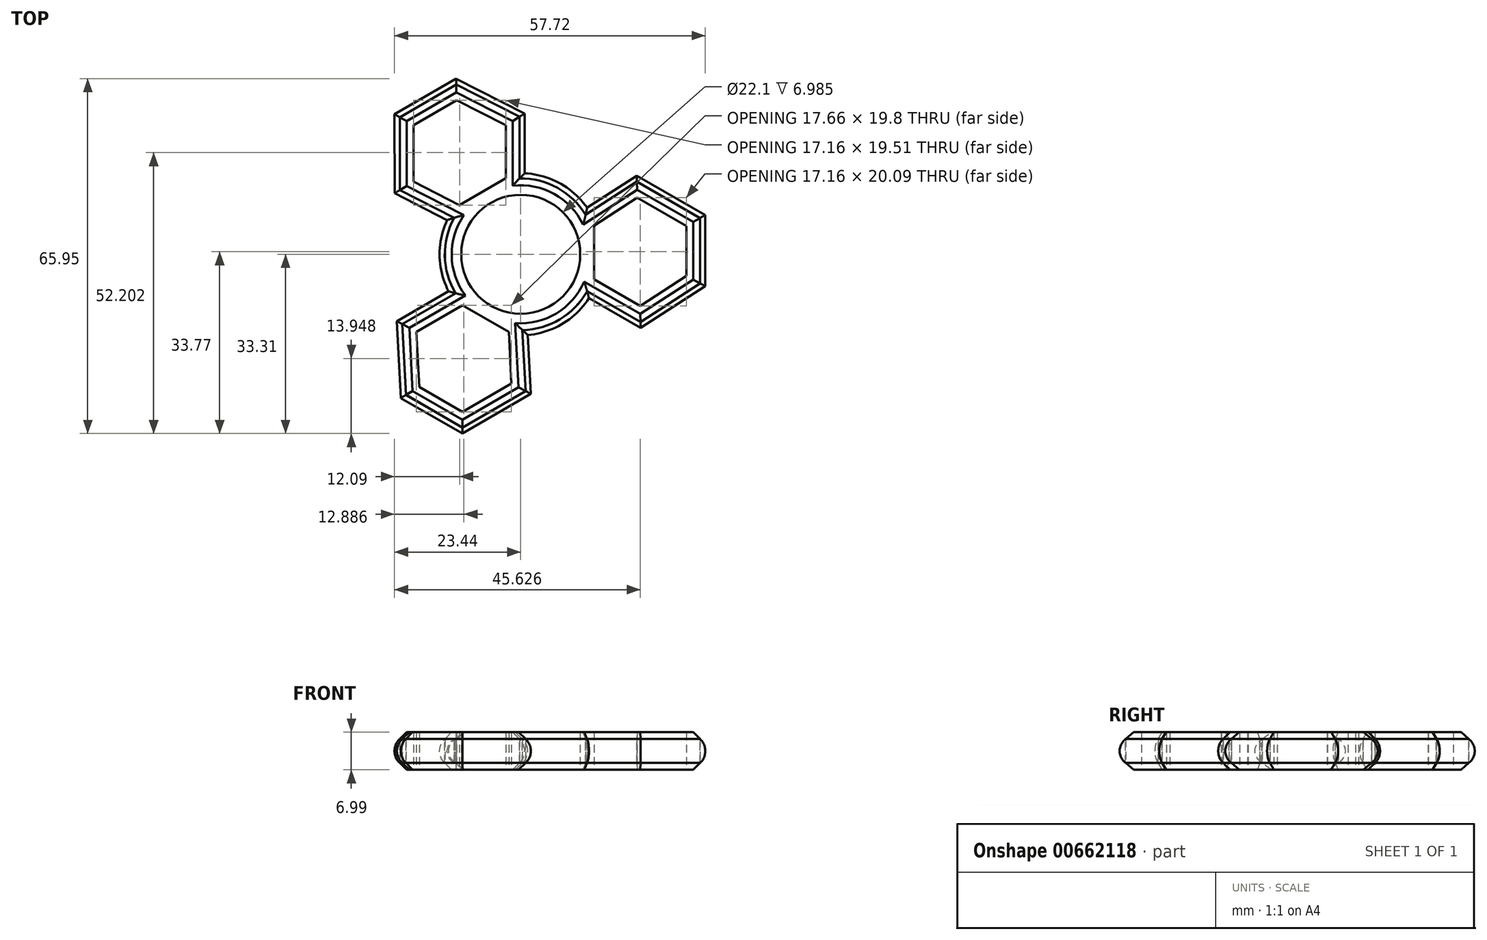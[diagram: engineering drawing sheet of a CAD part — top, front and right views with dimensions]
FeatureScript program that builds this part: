
annotation { "Feature Type Name" : "Feature", "Feature Type Description" : "" }
export const myFeature = defineFeature(function(context is Context, id is Id, definition is map)
    precondition{}
    {
        {
            var Q0;
            Q0=qCreatedBy(makeId("Top.planeOp"),FACE);
            var sketch = newSketch(context, id + "F0", { "sketchPlane" : qUnion([Q0])});
            skCircle(sketch, "E0", {"center": v(0, 0) * mm, "radius": 11.05 * mm});
            skLineSegment(sketch, "E1.0", {"start": v(21.64, 10.5) * mm, "end": v(30.75, 5.26) * mm});
            skLineSegment(sketch, "E1.1", {"start": v(30.75, 5.26) * mm, "end": v(30.76, -4.01) * mm});
            skLineSegment(sketch, "E1.2", {"start": v(30.76, -4.01) * mm, "end": v(22.17, -9.58) * mm});
            skLineSegment(sketch, "E1.3", {"start": v(22.17, -9.58) * mm, "end": v(13.62, -4.66) * mm});
            skLineSegment(sketch, "E1.4", {"start": v(13.62, -4.66) * mm, "end": v(13.6, 5.3) * mm});
            skLineSegment(sketch, "E1.5", {"start": v(13.6, 5.3) * mm, "end": v(21.64, 10.5) * mm});
            skLineSegment(sketch, "E2.1.0", {"start": v(-11.4, 9.14) * mm, "end": v(-19.92, 13.49) * mm});
            skLineSegment(sketch, "E2.1.1", {"start": v(-2.77, 14.13) * mm, "end": v(-11.4, 9.14) * mm});
            skLineSegment(sketch, "E2.1.2", {"start": v(-2.78, 24) * mm, "end": v(-2.77, 14.13) * mm});
            skLineSegment(sketch, "E2.1.3", {"start": v(-11.9, 28.65) * mm, "end": v(-2.78, 24) * mm});
            skLineSegment(sketch, "E2.1.4", {"start": v(-19.93, 24) * mm, "end": v(-11.9, 28.65) * mm});
            skLineSegment(sketch, "E2.1.5", {"start": v(-19.92, 13.49) * mm, "end": v(-19.93, 24) * mm});
            skLineSegment(sketch, "E2.2.0", {"start": v(-2.22, -14.43) * mm, "end": v(-1.72, -24) * mm});
            skLineSegment(sketch, "E2.2.1", {"start": v(-10.85, -9.46) * mm, "end": v(-2.22, -14.43) * mm});
            skLineSegment(sketch, "E2.2.2", {"start": v(-19.38, -14.4) * mm, "end": v(-10.85, -9.46) * mm});
            skLineSegment(sketch, "E2.2.3", {"start": v(-18.86, -24.64) * mm, "end": v(-19.38, -14.4) * mm});
            skLineSegment(sketch, "E2.2.4", {"start": v(-10.82, -29.26) * mm, "end": v(-18.86, -24.64) * mm});
            skLineSegment(sketch, "E2.2.5", {"start": v(-1.72, -24) * mm, "end": v(-10.82, -29.26) * mm});
            skLineSegment(sketch, "E3.0", {"start": v(21.56, 13.48) * mm, "end": v(33.3, 6.73) * mm});
            skLineSegment(sketch, "E3.1", {"start": v(33.3, -5.4) * mm, "end": v(22.25, -12.56) * mm});
            skLineSegment(sketch, "E3.2", {"start": v(22.25, -12.56) * mm, "end": v(12.32, -6.85) * mm});
            skLineSegment(sketch, "E3.3", {"start": v(33.3, 6.73) * mm, "end": v(33.3, -5.4) * mm});
            skLineSegment(sketch, "E3.5", {"start": v(12.05, 7.32) * mm, "end": v(21.56, 13.48) * mm});
            skLineSegment(sketch, "E4.0", {"start": v(-21.32, -26.15) * mm, "end": v(-22, -12.99) * mm});
            skLineSegment(sketch, "E4.2", {"start": v(0.31, -14.1) * mm, "end": v(0.9, -25.41) * mm});
            skLineSegment(sketch, "E4.3", {"start": v(-22, -12.99) * mm, "end": v(-12.1, -7.25) * mm});
            skLineSegment(sketch, "E4.4", {"start": v(0.9, -25.41) * mm, "end": v(-10.82, -32.2) * mm});
            skLineSegment(sketch, "E4.5", {"start": v(-10.82, -32.2) * mm, "end": v(-21.32, -26.15) * mm});
            skLineSegment(sketch, "E5.0", {"start": v(-11.98, 31.54) * mm, "end": v(-0.25, 25.55) * mm});
            skLineSegment(sketch, "E5.2", {"start": v(-12.36, 6.78) * mm, "end": v(-22.45, 11.93) * mm});
            skLineSegment(sketch, "E5.3", {"start": v(-0.25, 25.55) * mm, "end": v(-0.23, 14.1) * mm});
            skLineSegment(sketch, "E5.4", {"start": v(-22.45, 11.93) * mm, "end": v(-22.47, 25.47) * mm});
            skLineSegment(sketch, "E5.5", {"start": v(-22.47, 25.47) * mm, "end": v(-11.98, 31.54) * mm});
            skArc(sketch, "E6.0", {"start": v(12.05, 7.32) * mm, "mid": v(6.81, 12.34) * mm, "end": v(-0.23, 14.1) * mm});
            skArc(sketch, "E7.trimOffspring", {"start": v(0.31, -14.1) * mm, "mid": v(7.28, -12.07) * mm, "end": v(12.32, -6.85) * mm});
            skArc(sketch, "E8.trimOffspring", {"start": v(-12.36, 6.78) * mm, "mid": v(-14.1, -0.27) * mm, "end": v(-12.1, -7.25) * mm});
            skSolve(sketch);
        }
        {
            var Q0;
            Q0=makeQuery(id+"F0.imprint","IMPRINT",FACE,{"disambiguationData":[TD([[makeQuery(id+"F0.imprint","IMPRINT",EDGE,{"derivedFrom":sQuery(id+"F0.wireOp",EDGE,"E0")}),-1.0]])]});
            extrude(context, id + "F1", {"entities" : qUnion([Q0]), "depth" : 7 * mm, "offsetDistance" : 25.4 * mm});
        }
        {
            var Q0;
            Q0=makeQuery(id+"F1.opExtrude","CAP_EDGE",EDGE,{"disambiguationData":[OSD([sQuery(id+"F0.wireOp",EDGE,"E4.5")])],"isStart":false});
            var Q1;
            Q1=makeQuery(id+"F1.opExtrude","CAP_EDGE",EDGE,{"disambiguationData":[OSD([sQuery(id+"F0.wireOp",EDGE,"E4.4")])],"isStart":false});
            var Q2;
            Q2=makeQuery(id+"F1.opExtrude","CAP_EDGE",EDGE,{"disambiguationData":[OSD([sQuery(id+"F0.wireOp",EDGE,"E4.2")])],"isStart":false});
            var Q3;
            Q3=makeQuery(id+"F1.opExtrude","CAP_EDGE",EDGE,{"disambiguationData":[OSD([sQuery(id+"F0.wireOp",EDGE,"E7.trimOffspring")])],"isStart":false});
            var Q4;
            Q4=makeQuery(id+"F1.opExtrude","CAP_EDGE",EDGE,{"disambiguationData":[OSD([sQuery(id+"F0.wireOp",EDGE,"E3.2")])],"isStart":false});
            var Q5;
            Q5=makeQuery(id+"F1.opExtrude","CAP_EDGE",EDGE,{"disambiguationData":[OSD([sQuery(id+"F0.wireOp",EDGE,"E3.1")])],"isStart":false});
            var Q6;
            Q6=makeQuery(id+"F1.opExtrude","CAP_EDGE",EDGE,{"disambiguationData":[OSD([sQuery(id+"F0.wireOp",EDGE,"E3.3")])],"isStart":false});
            var Q7;
            Q7=makeQuery(id+"F1.opExtrude","CAP_EDGE",EDGE,{"disambiguationData":[OSD([sQuery(id+"F0.wireOp",EDGE,"E3.0")])],"isStart":false});
            var Q8;
            Q8=makeQuery(id+"F1.opExtrude","CAP_EDGE",EDGE,{"disambiguationData":[OSD([sQuery(id+"F0.wireOp",EDGE,"E3.5")])],"isStart":false});
            var Q9;
            Q9=makeQuery(id+"F1.opExtrude","CAP_EDGE",EDGE,{"disambiguationData":[OSD([sQuery(id+"F0.wireOp",EDGE,"E6.0")])],"isStart":false});
            var Q10;
            Q10=makeQuery(id+"F1.opExtrude","CAP_EDGE",EDGE,{"disambiguationData":[OSD([sQuery(id+"F0.wireOp",EDGE,"E5.3")])],"isStart":false});
            var Q11;
            Q11=makeQuery(id+"F1.opExtrude","CAP_EDGE",EDGE,{"disambiguationData":[OSD([sQuery(id+"F0.wireOp",EDGE,"E5.0")])],"isStart":false});
            var Q12;
            Q12=makeQuery(id+"F1.opExtrude","CAP_EDGE",EDGE,{"disambiguationData":[OSD([sQuery(id+"F0.wireOp",EDGE,"E5.5")])],"isStart":false});
            var Q13;
            Q13=makeQuery(id+"F1.opExtrude","CAP_EDGE",EDGE,{"disambiguationData":[OSD([sQuery(id+"F0.wireOp",EDGE,"E5.4")])],"isStart":false});
            var Q14;
            Q14=makeQuery(id+"F1.opExtrude","CAP_EDGE",EDGE,{"disambiguationData":[OSD([sQuery(id+"F0.wireOp",EDGE,"E5.2")])],"isStart":false});
            var Q15;
            Q15=makeQuery(id+"F1.opExtrude","CAP_EDGE",EDGE,{"disambiguationData":[OSD([sQuery(id+"F0.wireOp",EDGE,"E8.trimOffspring")])],"isStart":false});
            var Q16;
            Q16=makeQuery(id+"F1.opExtrude","CAP_EDGE",EDGE,{"disambiguationData":[OSD([sQuery(id+"F0.wireOp",EDGE,"E4.3")])],"isStart":false});
            var Q17;
            Q17=makeQuery(id+"F1.opExtrude","CAP_EDGE",EDGE,{"disambiguationData":[OSD([sQuery(id+"F0.wireOp",EDGE,"E4.0")])],"isStart":false});
            chamfer(context, id + "F2", {"entities" : qUnion([Q0, Q1, Q2, Q3, Q4, Q5, Q6, Q7, Q8, Q9, Q10, Q11, Q12, Q13, Q14, Q15, Q16, Q17]), "width" : 1.27 * mm, "tangentPropagation" : true});
        }
        {
            var Q0;
            Q0=makeQuery(id+"F1.opExtrude","CAP_EDGE",EDGE,{"disambiguationData":[OSD([sQuery(id+"F0.wireOp",EDGE,"E5.4")])],"isStart":true});
            var Q1;
            Q1=makeQuery(id+"F1.opExtrude","CAP_EDGE",EDGE,{"disambiguationData":[OSD([sQuery(id+"F0.wireOp",EDGE,"E5.5")])],"isStart":true});
            var Q2;
            Q2=makeQuery(id+"F1.opExtrude","CAP_EDGE",EDGE,{"disambiguationData":[OSD([sQuery(id+"F0.wireOp",EDGE,"E5.2")])],"isStart":true});
            var Q3;
            Q3=makeQuery(id+"F1.opExtrude","CAP_EDGE",EDGE,{"disambiguationData":[OSD([sQuery(id+"F0.wireOp",EDGE,"E8.trimOffspring")])],"isStart":true});
            var Q4;
            Q4=makeQuery(id+"F1.opExtrude","CAP_EDGE",EDGE,{"disambiguationData":[OSD([sQuery(id+"F0.wireOp",EDGE,"E4.3")])],"isStart":true});
            var Q5;
            Q5=makeQuery(id+"F1.opExtrude","CAP_EDGE",EDGE,{"disambiguationData":[OSD([sQuery(id+"F0.wireOp",EDGE,"E4.0")])],"isStart":true});
            var Q6;
            Q6=makeQuery(id+"F1.opExtrude","CAP_EDGE",EDGE,{"disambiguationData":[OSD([sQuery(id+"F0.wireOp",EDGE,"E5.0")])],"isStart":true});
            var Q7;
            Q7=makeQuery(id+"F1.opExtrude","CAP_EDGE",EDGE,{"disambiguationData":[OSD([sQuery(id+"F0.wireOp",EDGE,"E5.3")])],"isStart":true});
            var Q8;
            Q8=makeQuery(id+"F1.opExtrude","CAP_EDGE",EDGE,{"disambiguationData":[OSD([sQuery(id+"F0.wireOp",EDGE,"E6.0")])],"isStart":true});
            var Q9;
            Q9=makeQuery(id+"F1.opExtrude","CAP_EDGE",EDGE,{"disambiguationData":[OSD([sQuery(id+"F0.wireOp",EDGE,"E3.5")])],"isStart":true});
            var Q10;
            Q10=makeQuery(id+"F1.opExtrude","CAP_EDGE",EDGE,{"disambiguationData":[OSD([sQuery(id+"F0.wireOp",EDGE,"E3.0")])],"isStart":true});
            var Q11;
            Q11=makeQuery(id+"F1.opExtrude","CAP_EDGE",EDGE,{"disambiguationData":[OSD([sQuery(id+"F0.wireOp",EDGE,"E3.3")])],"isStart":true});
            var Q12;
            Q12=makeQuery(id+"F1.opExtrude","CAP_EDGE",EDGE,{"disambiguationData":[OSD([sQuery(id+"F0.wireOp",EDGE,"E3.1")])],"isStart":true});
            var Q13;
            Q13=makeQuery(id+"F1.opExtrude","CAP_EDGE",EDGE,{"disambiguationData":[OSD([sQuery(id+"F0.wireOp",EDGE,"E3.2")])],"isStart":true});
            var Q14;
            Q14=makeQuery(id+"F1.opExtrude","CAP_EDGE",EDGE,{"disambiguationData":[OSD([sQuery(id+"F0.wireOp",EDGE,"E7.trimOffspring")])],"isStart":true});
            var Q15;
            Q15=makeQuery(id+"F1.opExtrude","CAP_EDGE",EDGE,{"disambiguationData":[OSD([sQuery(id+"F0.wireOp",EDGE,"E4.2")])],"isStart":true});
            var Q16;
            Q16=makeQuery(id+"F1.opExtrude","CAP_EDGE",EDGE,{"disambiguationData":[OSD([sQuery(id+"F0.wireOp",EDGE,"E4.4")])],"isStart":true});
            var Q17;
            Q17=makeQuery(id+"F1.opExtrude","CAP_EDGE",EDGE,{"disambiguationData":[OSD([sQuery(id+"F0.wireOp",EDGE,"E4.5")])],"isStart":true});
            chamfer(context, id + "F3", {"entities" : qUnion([Q0, Q1, Q2, Q3, Q4, Q5, Q6, Q7, Q8, Q9, Q10, Q11, Q12, Q13, Q14, Q15, Q16, Q17]), "width" : 1.27 * mm, "tangentPropagation" : true});
        }
        {
            var Q0;
            Q0=qCreatedBy(makeId("Front.planeOp"),FACE);
            var sketch = newSketch(context, id + "F4", { "sketchPlane" : qUnion([Q0])});
            skArc(sketch, "E9", {"start": v(33.3, 1.27) * mm, "mid": v(34.27, 3.5) * mm, "end": v(33.3, 5.71) * mm});
            skLineSegment(sketch, "E10", {"start": v(33.3, 5.71) * mm, "end": v(33.3, 1.27) * mm});
            skSolve(sketch);
        }
        {
            var Q0;
            Q0=makeQuery(id+"F4.imprint","IMPRINT",FACE,{"disambiguationData":[TD([[makeQuery(id+"F4.imprint","IMPRINT",EDGE,{"derivedFrom":sQuery(id+"F4.wireOp",EDGE,"E9")}),1.0]])]});
            var Q1;
            {var subQ0=sQuery(id+"F0.wireOp",EDGE,"E3.3");Q1=makeQuery(id+"F2.opChamfer","BLEND_EDGE",EDGE,{"blendedFrom":[makeQuery(id+"F1.opExtrude","CAP_EDGE",EDGE,{"disambiguationData":[OSD([subQ0])],"isStart":false}),makeQuery(id+"F1.opExtrude","SWEPT_FACE",FACE,{"disambiguationData":[OSD([subQ0])]})],"blendedInto":[makeQuery(id+"F1.opExtrude","SWEPT_FACE",FACE,{"disambiguationData":[OSD([subQ0])]})]});}
            var Q2;
            {var subQ0=sQuery(id+"F0.wireOp",EDGE,"E3.1");Q2=makeQuery(id+"F2.opChamfer","BLEND_EDGE",EDGE,{"blendedFrom":[makeQuery(id+"F1.opExtrude","CAP_EDGE",EDGE,{"disambiguationData":[OSD([subQ0])],"isStart":false}),makeQuery(id+"F1.opExtrude","SWEPT_FACE",FACE,{"disambiguationData":[OSD([subQ0])]})],"blendedInto":[makeQuery(id+"F1.opExtrude","SWEPT_FACE",FACE,{"disambiguationData":[OSD([subQ0])]})]});}
            var Q3;
            {var subQ0=sQuery(id+"F0.wireOp",EDGE,"E3.2");Q3=makeQuery(id+"F2.opChamfer","BLEND_EDGE",EDGE,{"blendedFrom":[makeQuery(id+"F1.opExtrude","CAP_EDGE",EDGE,{"disambiguationData":[OSD([subQ0])],"isStart":false}),makeQuery(id+"F1.opExtrude","SWEPT_FACE",FACE,{"disambiguationData":[OSD([subQ0])]})],"blendedInto":[makeQuery(id+"F1.opExtrude","SWEPT_FACE",FACE,{"disambiguationData":[OSD([subQ0])]})]});}
            var Q4;
            {var subQ0=sQuery(id+"F0.wireOp",EDGE,"E7.trimOffspring");Q4=makeQuery(id+"F2.opChamfer","BLEND_EDGE",EDGE,{"blendedFrom":[makeQuery(id+"F1.opExtrude","CAP_EDGE",EDGE,{"disambiguationData":[OSD([subQ0])],"isStart":false}),makeQuery(id+"F1.opExtrude","SWEPT_FACE",FACE,{"disambiguationData":[OSD([subQ0])]})],"blendedInto":[makeQuery(id+"F1.opExtrude","SWEPT_FACE",FACE,{"disambiguationData":[OSD([subQ0])]})]});}
            var Q5;
            {var subQ0=sQuery(id+"F0.wireOp",EDGE,"E4.2");Q5=makeQuery(id+"F2.opChamfer","BLEND_EDGE",EDGE,{"blendedFrom":[makeQuery(id+"F1.opExtrude","CAP_EDGE",EDGE,{"disambiguationData":[OSD([subQ0])],"isStart":false}),makeQuery(id+"F1.opExtrude","SWEPT_FACE",FACE,{"disambiguationData":[OSD([subQ0])]})],"blendedInto":[makeQuery(id+"F1.opExtrude","SWEPT_FACE",FACE,{"disambiguationData":[OSD([subQ0])]})]});}
            var Q6;
            {var subQ0=sQuery(id+"F0.wireOp",EDGE,"E4.4");Q6=makeQuery(id+"F2.opChamfer","BLEND_EDGE",EDGE,{"blendedFrom":[makeQuery(id+"F1.opExtrude","CAP_EDGE",EDGE,{"disambiguationData":[OSD([subQ0])],"isStart":false}),makeQuery(id+"F1.opExtrude","SWEPT_FACE",FACE,{"disambiguationData":[OSD([subQ0])]})],"blendedInto":[makeQuery(id+"F1.opExtrude","SWEPT_FACE",FACE,{"disambiguationData":[OSD([subQ0])]})]});}
            var Q7;
            {var subQ0=sQuery(id+"F0.wireOp",EDGE,"E4.5");Q7=makeQuery(id+"F2.opChamfer","BLEND_EDGE",EDGE,{"blendedFrom":[makeQuery(id+"F1.opExtrude","CAP_EDGE",EDGE,{"disambiguationData":[OSD([subQ0])],"isStart":false}),makeQuery(id+"F1.opExtrude","SWEPT_FACE",FACE,{"disambiguationData":[OSD([subQ0])]})],"blendedInto":[makeQuery(id+"F1.opExtrude","SWEPT_FACE",FACE,{"disambiguationData":[OSD([subQ0])]})]});}
            var Q8;
            {var subQ0=sQuery(id+"F0.wireOp",EDGE,"E8.trimOffspring");Q8=makeQuery(id+"F2.opChamfer","BLEND_EDGE",EDGE,{"blendedFrom":[makeQuery(id+"F1.opExtrude","CAP_EDGE",EDGE,{"disambiguationData":[OSD([subQ0])],"isStart":false}),makeQuery(id+"F1.opExtrude","SWEPT_FACE",FACE,{"disambiguationData":[OSD([subQ0])]})],"blendedInto":[makeQuery(id+"F1.opExtrude","SWEPT_FACE",FACE,{"disambiguationData":[OSD([subQ0])]})]});}
            var Q9;
            {var subQ0=sQuery(id+"F0.wireOp",EDGE,"E4.3");Q9=makeQuery(id+"F2.opChamfer","BLEND_EDGE",EDGE,{"blendedFrom":[makeQuery(id+"F1.opExtrude","CAP_EDGE",EDGE,{"disambiguationData":[OSD([subQ0])],"isStart":false}),makeQuery(id+"F1.opExtrude","SWEPT_FACE",FACE,{"disambiguationData":[OSD([subQ0])]})],"blendedInto":[makeQuery(id+"F1.opExtrude","SWEPT_FACE",FACE,{"disambiguationData":[OSD([subQ0])]})]});}
            var Q10;
            {var subQ0=sQuery(id+"F0.wireOp",EDGE,"E4.0");Q10=makeQuery(id+"F2.opChamfer","BLEND_EDGE",EDGE,{"blendedFrom":[makeQuery(id+"F1.opExtrude","CAP_EDGE",EDGE,{"disambiguationData":[OSD([subQ0])],"isStart":false}),makeQuery(id+"F1.opExtrude","SWEPT_FACE",FACE,{"disambiguationData":[OSD([subQ0])]})],"blendedInto":[makeQuery(id+"F1.opExtrude","SWEPT_FACE",FACE,{"disambiguationData":[OSD([subQ0])]})]});}
            var Q11;
            {var subQ0=sQuery(id+"F0.wireOp",EDGE,"E5.2");Q11=makeQuery(id+"F2.opChamfer","BLEND_EDGE",EDGE,{"blendedFrom":[makeQuery(id+"F1.opExtrude","CAP_EDGE",EDGE,{"disambiguationData":[OSD([subQ0])],"isStart":false}),makeQuery(id+"F1.opExtrude","SWEPT_FACE",FACE,{"disambiguationData":[OSD([subQ0])]})],"blendedInto":[makeQuery(id+"F1.opExtrude","SWEPT_FACE",FACE,{"disambiguationData":[OSD([subQ0])]})]});}
            var Q12;
            {var subQ0=sQuery(id+"F0.wireOp",EDGE,"E5.4");Q12=makeQuery(id+"F2.opChamfer","BLEND_EDGE",EDGE,{"blendedFrom":[makeQuery(id+"F1.opExtrude","CAP_EDGE",EDGE,{"disambiguationData":[OSD([subQ0])],"isStart":false}),makeQuery(id+"F1.opExtrude","SWEPT_FACE",FACE,{"disambiguationData":[OSD([subQ0])]})],"blendedInto":[makeQuery(id+"F1.opExtrude","SWEPT_FACE",FACE,{"disambiguationData":[OSD([subQ0])]})]});}
            var Q13;
            {var subQ0=sQuery(id+"F0.wireOp",EDGE,"E5.5");Q13=makeQuery(id+"F2.opChamfer","BLEND_EDGE",EDGE,{"blendedFrom":[makeQuery(id+"F1.opExtrude","CAP_EDGE",EDGE,{"disambiguationData":[OSD([subQ0])],"isStart":false}),makeQuery(id+"F1.opExtrude","SWEPT_FACE",FACE,{"disambiguationData":[OSD([subQ0])]})],"blendedInto":[makeQuery(id+"F1.opExtrude","SWEPT_FACE",FACE,{"disambiguationData":[OSD([subQ0])]})]});}
            var Q14;
            {var subQ0=sQuery(id+"F0.wireOp",EDGE,"E5.0");Q14=makeQuery(id+"F2.opChamfer","BLEND_EDGE",EDGE,{"blendedFrom":[makeQuery(id+"F1.opExtrude","CAP_EDGE",EDGE,{"disambiguationData":[OSD([subQ0])],"isStart":false}),makeQuery(id+"F1.opExtrude","SWEPT_FACE",FACE,{"disambiguationData":[OSD([subQ0])]})],"blendedInto":[makeQuery(id+"F1.opExtrude","SWEPT_FACE",FACE,{"disambiguationData":[OSD([subQ0])]})]});}
            var Q15;
            {var subQ0=sQuery(id+"F0.wireOp",EDGE,"E5.3");Q15=makeQuery(id+"F2.opChamfer","BLEND_EDGE",EDGE,{"blendedFrom":[makeQuery(id+"F1.opExtrude","CAP_EDGE",EDGE,{"disambiguationData":[OSD([subQ0])],"isStart":false}),makeQuery(id+"F1.opExtrude","SWEPT_FACE",FACE,{"disambiguationData":[OSD([subQ0])]})],"blendedInto":[makeQuery(id+"F1.opExtrude","SWEPT_FACE",FACE,{"disambiguationData":[OSD([subQ0])]})]});}
            var Q16;
            {var subQ0=sQuery(id+"F0.wireOp",EDGE,"E6.0");Q16=makeQuery(id+"F2.opChamfer","BLEND_EDGE",EDGE,{"blendedFrom":[makeQuery(id+"F1.opExtrude","CAP_EDGE",EDGE,{"disambiguationData":[OSD([subQ0])],"isStart":false}),makeQuery(id+"F1.opExtrude","SWEPT_FACE",FACE,{"disambiguationData":[OSD([subQ0])]})],"blendedInto":[makeQuery(id+"F1.opExtrude","SWEPT_FACE",FACE,{"disambiguationData":[OSD([subQ0])]})]});}
            var Q17;
            {var subQ0=sQuery(id+"F0.wireOp",EDGE,"E3.5");Q17=makeQuery(id+"F2.opChamfer","BLEND_EDGE",EDGE,{"blendedFrom":[makeQuery(id+"F1.opExtrude","CAP_EDGE",EDGE,{"disambiguationData":[OSD([subQ0])],"isStart":false}),makeQuery(id+"F1.opExtrude","SWEPT_FACE",FACE,{"disambiguationData":[OSD([subQ0])]})],"blendedInto":[makeQuery(id+"F1.opExtrude","SWEPT_FACE",FACE,{"disambiguationData":[OSD([subQ0])]})]});}
            var Q18;
            {var subQ0=sQuery(id+"F0.wireOp",EDGE,"E3.0");Q18=makeQuery(id+"F2.opChamfer","BLEND_EDGE",EDGE,{"blendedFrom":[makeQuery(id+"F1.opExtrude","CAP_EDGE",EDGE,{"disambiguationData":[OSD([subQ0])],"isStart":false}),makeQuery(id+"F1.opExtrude","SWEPT_FACE",FACE,{"disambiguationData":[OSD([subQ0])]})],"blendedInto":[makeQuery(id+"F1.opExtrude","SWEPT_FACE",FACE,{"disambiguationData":[OSD([subQ0])]})]});}
            sweep(context, id + "F5", {"profiles" : qUnion([Q0]), "path" : qUnion([Q1, Q2, Q3, Q4, Q5, Q6, Q7, Q8, Q9, Q10, Q11, Q12, Q13, Q14, Q15, Q16, Q17, Q18])});
        }
    });
